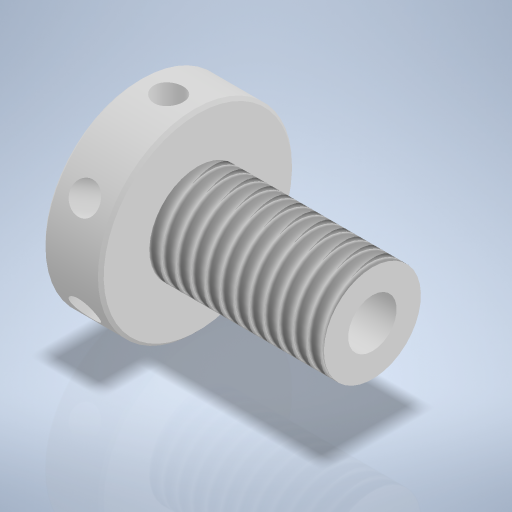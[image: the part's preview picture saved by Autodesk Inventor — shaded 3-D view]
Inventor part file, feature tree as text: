
AUTODESK INVENTOR PART (.ipt)
format: ipt  version: 2024 (Build 280153000, 153)  size: 332,800 bytes
history: native  units: mm
features: sketch x3, hole x2, revolve x1, thread x1, plane x1, pattern_circular x1, chamfer x1
ambient origin geometry x8: Origin, YZ Plane, XZ Plane, XY Plane, X Axis, Y Axis, Z Axis, Center Point
bodies: Volumenkörper1 (feature_tree)
feature tree (10):
  revolve  "Umdrehung1"
  hole  "Bohrung1"  [1 undecoded]
  thread  "Gewinde1"  [1 undecoded]
  plane  "Arbeitsebene1"
  hole  "Bohrung2"  [1 undecoded]
  pattern_circular  "Runde Anordnung1"  [2 undecoded]
  chamfer  "Fasen1"  Distance=10.0mm
  sketch  "Skizze1"  dims[d0=20.0mm d1=10.0mm d2=6.0mm]
  sketch  "Skizze2"  dims[d3=18.0mm d4=90.0deg]
  sketch  "Skizze3"  dims[d5=5.0mm d6=6.0mm d7=4.0mm d8=2.0mm d9=90.0deg d10=25.0mm d11=0.0mm d12=18.0mm d13=0.0mm d14=10.0mm d15=3.0mm d16=3.0mm d17=6.0mm d18=4.0mm d19=2.0mm d20=90.0deg d21=6.0mm d22=0.0mm d23=60.0mm d24=360.0deg d26=0.3mm d27=2.0mm d28=45.0deg]
note: 5 required parameter values undecoded (feature->parameter linkage not recoverable at this tier; creation-order binding heuristic only, values carry confidence <= 0.55)
